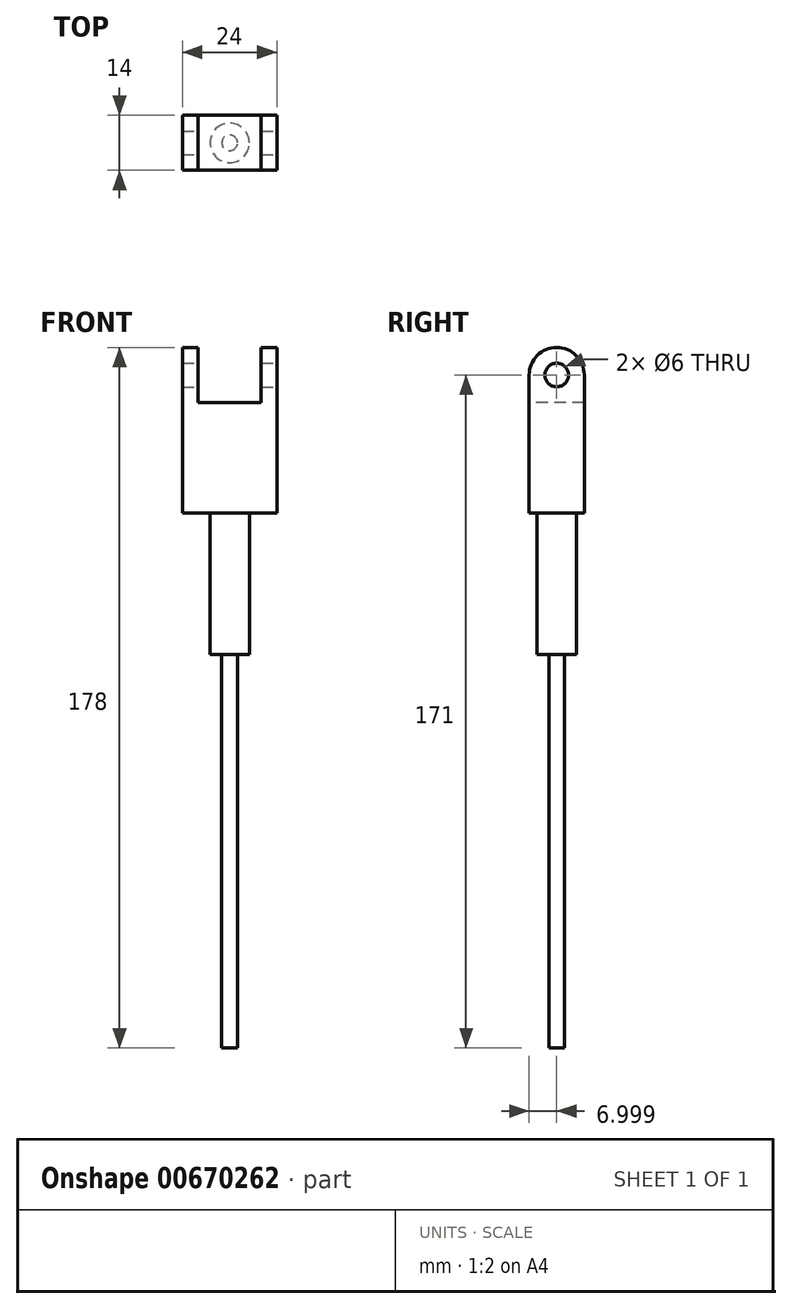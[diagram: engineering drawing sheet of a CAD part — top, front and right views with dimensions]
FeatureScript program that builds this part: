
annotation { "Feature Type Name" : "Feature", "Feature Type Description" : "" }
export const myFeature = defineFeature(function(context is Context, id is Id, definition is map)
    precondition{}
    {
        {
            var Q0;
            Q0=qCreatedBy(makeId("Top.planeOp"),FACE);
            var sketch = newSketch(context, id + "F0", { "sketchPlane" : qUnion([Q0])});
            skLineSegment(sketch, "E0.bottom", {"start": v(-5.97, 6.04) * mm, "end": v(18.03, 6.04) * mm});
            skLineSegment(sketch, "E0.top", {"start": v(-5.97, -7.96) * mm, "end": v(18.03, -7.96) * mm});
            skLineSegment(sketch, "E0.left", {"start": v(-5.97, 6.04) * mm, "end": v(-5.97, -7.96) * mm});
            skLineSegment(sketch, "E0.right", {"start": v(18.03, 6.04) * mm, "end": v(18.03, -7.96) * mm});
            skSolve(sketch);
        }
        {
            var Q0;
            Q0=makeQuery(id+"F0.imprint","IMPRINT",FACE,{"disambiguationData":[TD([[makeQuery(id+"F0.imprint","IMPRINT",EDGE,{"derivedFrom":sQuery(id+"F0.wireOp",EDGE,"E0.bottom")}),-1.0]])]});
            extrude(context, id + "F1", {"entities" : qUnion([Q0]), "depth" : -28 * mm, "offsetDistance" : 25 * mm});
        }
        {
            var Q0;
            Q0=makeQuery(id+"F1.opExtrude","CAP_FACE",FACE,{"disambiguationData":[OSD([sQuery(id+"F0.wireOp",EDGE,"E0.bottom"),sQuery(id+"F0.wireOp",EDGE,"E0.top"),sQuery(id+"F0.wireOp",EDGE,"E0.left"),sQuery(id+"F0.wireOp",EDGE,"E0.right")])],"isStart":true});
            var sketch = newSketch(context, id + "F2", { "sketchPlane" : qUnion([Q0])});
            skLineSegment(sketch, "E1.bottom", {"start": v(-5.97, 6.04) * mm, "end": v(-1.97, 6.04) * mm});
            skLineSegment(sketch, "E1.top", {"start": v(-5.97, -7.96) * mm, "end": v(-1.97, -7.96) * mm});
            skLineSegment(sketch, "E1.left", {"start": v(-5.97, 6.04) * mm, "end": v(-5.97, -7.96) * mm});
            skLineSegment(sketch, "E1.right", {"start": v(-1.97, 6.04) * mm, "end": v(-1.97, -7.96) * mm});
            skLineSegment(sketch, "E2.bottom", {"start": v(18.03, 6.04) * mm, "end": v(14.03, 6.04) * mm});
            skLineSegment(sketch, "E2.top", {"start": v(18.03, -7.96) * mm, "end": v(14.03, -7.96) * mm});
            skLineSegment(sketch, "E2.left", {"start": v(18.03, 6.04) * mm, "end": v(18.03, -7.96) * mm});
            skLineSegment(sketch, "E2.right", {"start": v(14.03, 6.04) * mm, "end": v(14.03, -7.96) * mm});
            skSolve(sketch);
        }
        {
            var Q0;
            Q0=makeQuery(id+"F2.imprint","IMPRINT",FACE,{"disambiguationData":[TD([[makeQuery(id+"F2.imprint","IMPRINT",EDGE,{"derivedFrom":sQuery(id+"F2.wireOp",EDGE,"E1.bottom")}),-1.0]])]});
            var Q1;
            Q1=makeQuery(id+"F2.imprint","IMPRINT",FACE,{"disambiguationData":[TD([[makeQuery(id+"F2.imprint","IMPRINT",EDGE,{"derivedFrom":sQuery(id+"F2.wireOp",EDGE,"E2.bottom")}),-1.0]])]});
            extrude(context, id + "F3", {"entities" : qUnion([Q0, Q1]), "operationType" : NewBodyOperationType.ADD, "depth" : 14 * mm, "offsetDistance" : 25 * mm});
        }
        {
            var Q0;
            Q0=makeQuery(id+"F3.boolean.opBoolean","MERGE",FACE,{"derivedFrom":[makeQuery(id+"F1.opExtrude","SWEPT_FACE",FACE,{"disambiguationData":[OSD([sQuery(id+"F0.wireOp",EDGE,"E0.right")])]}),makeQuery(id+"F3.opExtrude","SWEPT_FACE",FACE,{"disambiguationData":[OSD([sQuery(id+"F2.wireOp",EDGE,"E2.left")])]})]});
            var sketch = newSketch(context, id + "F4", { "sketchPlane" : qUnion([Q0])});
            skCircle(sketch, "E3", {"center": v(-0.96, 7) * mm, "radius": 0.94 * mm});
            skArc(sketch, "E4", {"start": v(6.04, 7) * mm, "mid": v(-0.96, 14) * mm, "end": v(-7.96, 7) * mm});
            skSolve(sketch);
        }
        {
            var Q0;
            Q0=sQuery(id+"F4.wireOp",VERTEX,"E3.center");
            var Q1;
            Q1=makeQuery(id+"F1.opExtrude","SWEPT_BODY",BODY,{"disambiguationData":[OSD([sQuery(id+"F0.wireOp",EDGE,"E0.bottom"),sQuery(id+"F0.wireOp",EDGE,"E0.top"),sQuery(id+"F0.wireOp",EDGE,"E0.left"),sQuery(id+"F0.wireOp",EDGE,"E0.right")])]});
            hole(context, id + "F5", {"style" : HoleStyle.SIMPLE, "endStyle" : HoleEndStyle.THROUGH, "holeDiameter" : 6 * mm, "majorDiameter" : 5 * mm, "isTappedThrough" : true, "tappedDepth" : 12 * mm, "tapClearance" : 3, "locations" : qUnion([Q0]), "scope" : qUnion([Q1])});
        }
        {
            var Q0;
            Q0=makeQuery(id+"F3.opExtrude","CAP_EDGE",EDGE,{"disambiguationData":[OSD([sQuery(id+"F2.wireOp",EDGE,"E2.top")])],"isStart":false});
            var Q1;
            Q1=makeQuery(id+"F3.opExtrude","CAP_EDGE",EDGE,{"disambiguationData":[OSD([sQuery(id+"F2.wireOp",EDGE,"E2.bottom")])],"isStart":false});
            var Q2;
            Q2=makeQuery(id+"F3.opExtrude","CAP_EDGE",EDGE,{"disambiguationData":[OSD([sQuery(id+"F2.wireOp",EDGE,"E1.bottom")])],"isStart":false});
            var Q3;
            Q3=makeQuery(id+"F3.opExtrude","CAP_EDGE",EDGE,{"disambiguationData":[OSD([sQuery(id+"F2.wireOp",EDGE,"E1.top")])],"isStart":false});
            fillet(context, id + "F6", {"entities" : qUnion([Q0, Q1, Q2, Q3]), "radius" : 7 * mm, "tangentPropagation" : true, "allowEdgeOverflow" : false});
        }
        {
            var Q0;
            Q0=makeQuery(id+"F1.opExtrude","CAP_FACE",FACE,{"disambiguationData":[OSD([sQuery(id+"F0.wireOp",EDGE,"E0.bottom"),sQuery(id+"F0.wireOp",EDGE,"E0.top"),sQuery(id+"F0.wireOp",EDGE,"E0.left"),sQuery(id+"F0.wireOp",EDGE,"E0.right")])],"isStart":false});
            var sketch = newSketch(context, id + "F7", { "sketchPlane" : qUnion([Q0])});
            skCircle(sketch, "E5", {"center": v(6.03, 0.96) * mm, "radius": 5 * mm});
            skSolve(sketch);
        }
        {
            var Q0;
            Q0=makeQuery(id+"F7.imprint","IMPRINT",FACE,{"disambiguationData":[TD([[makeQuery(id+"F7.imprint","IMPRINT",EDGE,{"derivedFrom":sQuery(id+"F7.wireOp",EDGE,"E5")}),1.0]])]});
            extrude(context, id + "F8", {"entities" : qUnion([Q0]), "operationType" : NewBodyOperationType.ADD, "depth" : 36 * mm, "offsetDistance" : 25 * mm});
        }
        {
            var Q0;
            Q0=makeQuery(id+"F8.opExtrude","CAP_FACE",FACE,{"disambiguationData":[OSD([sQuery(id+"F7.wireOp",EDGE,"E5")])],"isStart":false});
            var sketch = newSketch(context, id + "F9", { "sketchPlane" : qUnion([Q0])});
            skCircle(sketch, "E6", {"center": v(6.03, 0.96) * mm, "radius": 2 * mm});
            skSolve(sketch);
        }
        {
            var Q0;
            Q0=makeQuery(id+"F9.imprint","IMPRINT",FACE,{"disambiguationData":[TD([[makeQuery(id+"F9.imprint","IMPRINT",EDGE,{"derivedFrom":sQuery(id+"F9.wireOp",EDGE,"E6")}),1.0]])]});
            extrude(context, id + "F10", {"entities" : qUnion([Q0]), "operationType" : NewBodyOperationType.ADD, "depth" : 100 * mm, "offsetDistance" : 25 * mm});
        }
    });
